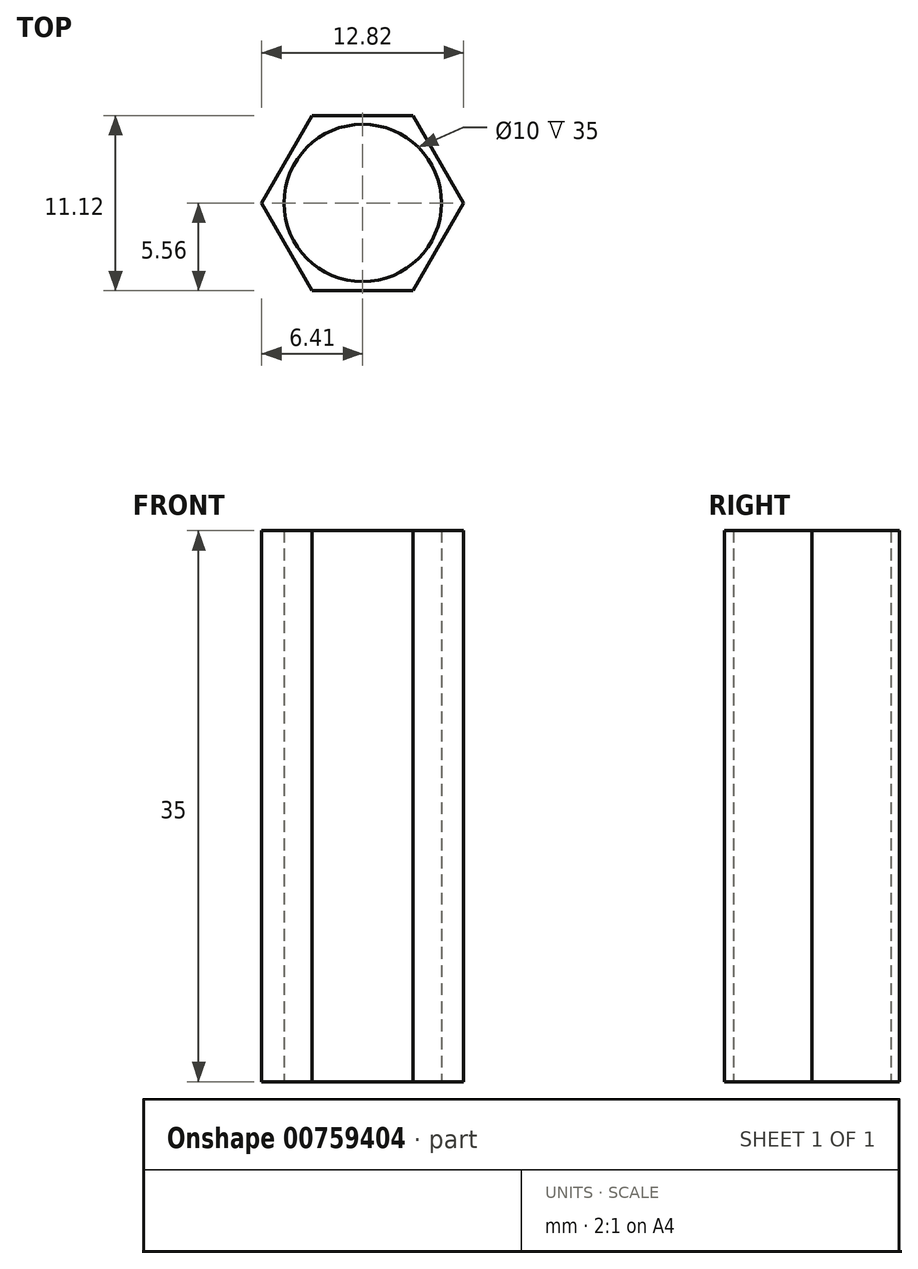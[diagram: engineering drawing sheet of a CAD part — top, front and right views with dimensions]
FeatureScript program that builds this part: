
annotation { "Feature Type Name" : "Feature", "Feature Type Description" : "" }
export const myFeature = defineFeature(function(context is Context, id is Id, definition is map)
    precondition{}
    {
        {
            var Q0;
            Q0=qCreatedBy(makeId("Top.planeOp"),FACE);
            var sketch = newSketch(context, id + "F0", { "sketchPlane" : qUnion([Q0])});
            skCircle(sketch, "E0.cCircle", {"center": v(0, 0) * mm, "radius": 5.55 * mm, "construction": true});
            skLineSegment(sketch, "E0.0", {"start": v(3.2, -5.55) * mm, "end": v(-3.2, -5.55) * mm});
            skLineSegment(sketch, "E0.1", {"start": v(-3.2, -5.55) * mm, "end": v(-6.41, 0) * mm});
            skLineSegment(sketch, "E0.2", {"start": v(-6.41, 0) * mm, "end": v(-3.2, 5.56) * mm});
            skLineSegment(sketch, "E0.3", {"start": v(-3.2, 5.55) * mm, "end": v(3.2, 5.56) * mm});
            skLineSegment(sketch, "E0.4", {"start": v(3.2, 5.56) * mm, "end": v(6.41, 0) * mm});
            skLineSegment(sketch, "E0.5", {"start": v(6.41, 0) * mm, "end": v(3.2, -5.56) * mm});
            skPoint(sketch, "E0.0.midPoint", {"position": v(0, -5.55) * mm});
            skCircle(sketch, "E1", {"center": v(0, 0) * mm, "radius": 5 * mm});
            skSolve(sketch);
        }
        {
            var Q0;
            Q0 = qSketchRegion(id + "F0", true);
            extrude(context, id + "F1", {"entities" : qUnion([Q0]), "endBound" : BoundingType.SYMMETRIC, "depth" : 35 * mm, "offsetDistance" : 25 * mm});
        }
    });
